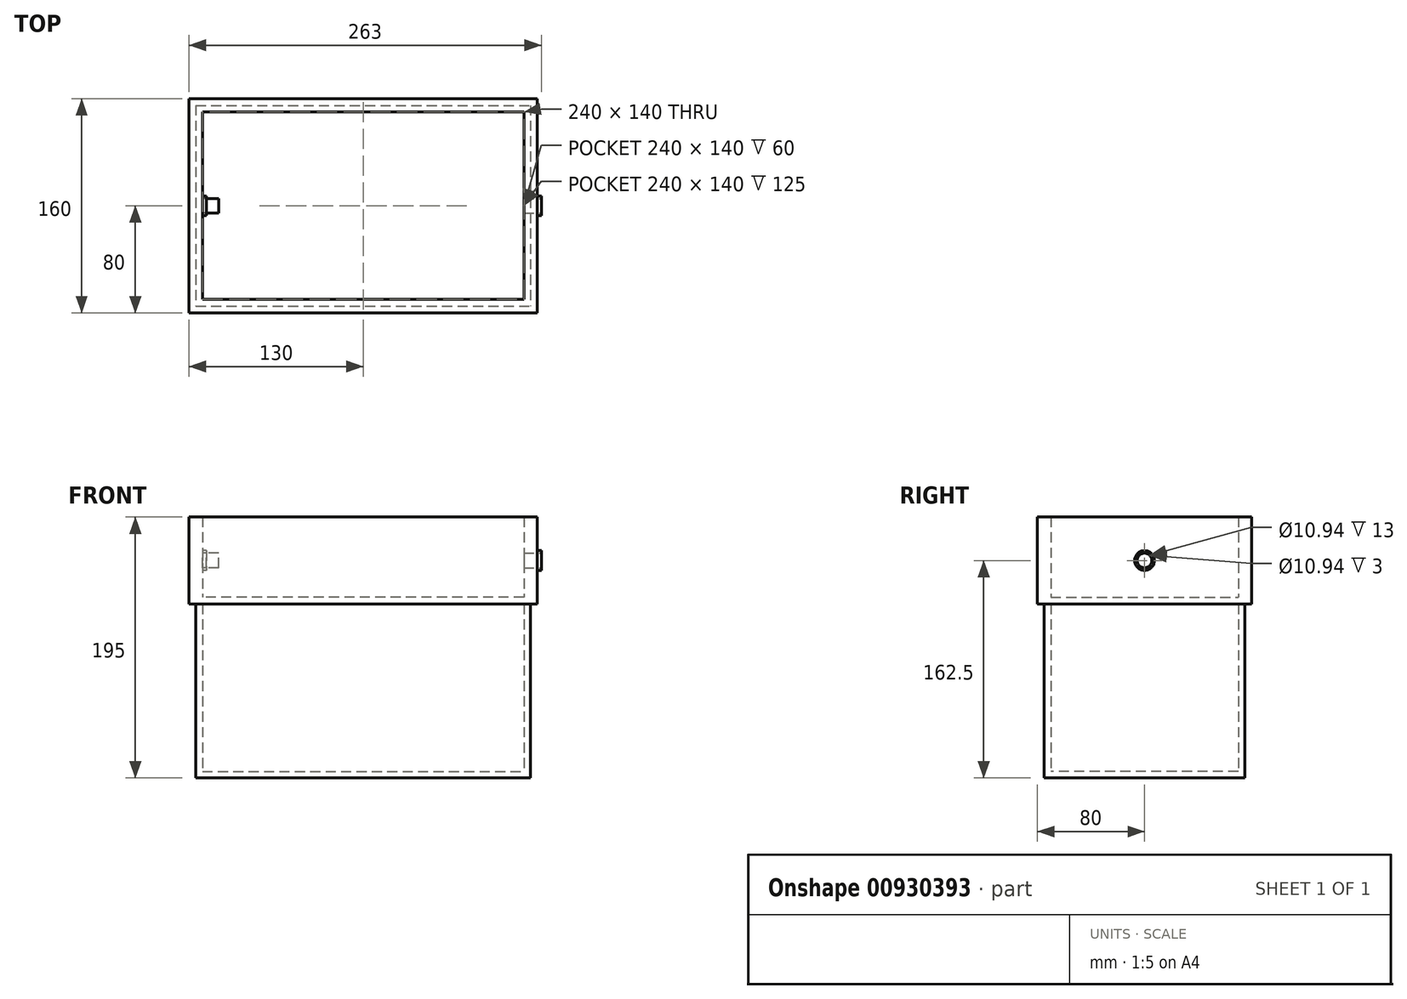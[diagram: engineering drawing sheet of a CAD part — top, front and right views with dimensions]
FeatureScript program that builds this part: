
annotation { "Feature Type Name" : "Feature", "Feature Type Description" : "" }
export const myFeature = defineFeature(function(context is Context, id is Id, definition is map)
    precondition{}
    {
        {
            var Q0;
            Q0=qCreatedBy(makeId("Top.planeOp"),FACE);
            var sketch = newSketch(context, id + "F0", { "sketchPlane" : qUnion([Q0])});
            skLineSegment(sketch, "E0.bottom", {"start": v(-125, 75) * mm, "end": v(125, 75) * mm});
            skLineSegment(sketch, "E0.top", {"start": v(-125, -75) * mm, "end": v(125, -75) * mm});
            skLineSegment(sketch, "E0.left", {"start": v(-125, 75) * mm, "end": v(-125, -75) * mm});
            skLineSegment(sketch, "E0.right", {"start": v(125, 75) * mm, "end": v(125, -75) * mm});
            skPoint(sketch, "E0.middle", {"position": v(0, 0) * mm});
            skSolve(sketch);
        }
        {
            var Q0;
            Q0 = qSketchRegion(id + "F0", true);
            extrude(context, id + "F1", {"entities" : qUnion([Q0]), "depth" : 5 * mm, "offsetDistance" : 25 * mm});
        }
        {
            var Q0;
            Q0=makeQuery(id+"F1.opExtrude","CAP_FACE",FACE,{"disambiguationData":[OSD([sQuery(id+"F0.wireOp",EDGE,"E0.bottom"),sQuery(id+"F0.wireOp",EDGE,"E0.top"),sQuery(id+"F0.wireOp",EDGE,"E0.left"),sQuery(id+"F0.wireOp",EDGE,"E0.right")])],"isStart":false});
            var sketch = newSketch(context, id + "F2", { "sketchPlane" : qUnion([Q0])});
            skLineSegment(sketch, "E1.bottom", {"start": v(-120, 70) * mm, "end": v(120, 70) * mm});
            skLineSegment(sketch, "E1.top", {"start": v(-120, -70) * mm, "end": v(120, -70) * mm});
            skLineSegment(sketch, "E1.left", {"start": v(-120, 70) * mm, "end": v(-120, -70) * mm});
            skLineSegment(sketch, "E1.right", {"start": v(120, 70) * mm, "end": v(120, -70) * mm});
            skPoint(sketch, "E1.middle", {"position": v(0, 0) * mm});
            skLineSegment(sketch, "E2.bottom", {"start": v(-125, 75) * mm, "end": v(125, 75) * mm});
            skLineSegment(sketch, "E2.top", {"start": v(-125, -75) * mm, "end": v(125, -75) * mm});
            skLineSegment(sketch, "E2.left", {"start": v(-125, 75) * mm, "end": v(-125, -75) * mm});
            skLineSegment(sketch, "E2.right", {"start": v(125, 75) * mm, "end": v(125, -75) * mm});
            skSolve(sketch);
        }
        {
            var Q0;
            Q0 = qSketchRegion(id + "F2", true);
            extrude(context, id + "F3", {"entities" : qUnion([Q0]), "operationType" : NewBodyOperationType.ADD, "depth" : 125 * mm, "offsetDistance" : 25 * mm});
        }
        {
            var Q0;
            Q0=makeQuery(id+"F3.opExtrude","CAP_FACE",FACE,{"disambiguationData":[OSD([sQuery(id+"F2.wireOp",EDGE,"E1.bottom"),sQuery(id+"F2.wireOp",EDGE,"E1.top"),sQuery(id+"F2.wireOp",EDGE,"E1.left"),sQuery(id+"F2.wireOp",EDGE,"E1.right"),sQuery(id+"F2.wireOp",EDGE,"E2.bottom"),sQuery(id+"F2.wireOp",EDGE,"E2.top"),sQuery(id+"F2.wireOp",EDGE,"E2.left"),sQuery(id+"F2.wireOp",EDGE,"E2.right")])],"isStart":false});
            var sketch = newSketch(context, id + "F4", { "sketchPlane" : qUnion([Q0])});
            skLineSegment(sketch, "E3.bottom", {"start": v(-130, 80) * mm, "end": v(130, 80) * mm});
            skLineSegment(sketch, "E3.top", {"start": v(-130, -80) * mm, "end": v(130, -80) * mm});
            skLineSegment(sketch, "E3.left", {"start": v(-130, 80) * mm, "end": v(-130, -80) * mm});
            skLineSegment(sketch, "E3.right", {"start": v(130, 80) * mm, "end": v(130, -80) * mm});
            skPoint(sketch, "E3.middle", {"position": v(0, 0) * mm});
            skSolve(sketch);
        }
        {
            var Q0;
            Q0 = qSketchRegion(id + "F4", true);
            extrude(context, id + "F5", {"entities" : qUnion([Q0]), "depth" : 5 * mm, "offsetDistance" : 25 * mm});
        }
        {
            var Q0;
            Q0=makeQuery(id+"F5.opExtrude","CAP_FACE",FACE,{"disambiguationData":[OSD([sQuery(id+"F4.wireOp",EDGE,"E3.bottom"),sQuery(id+"F4.wireOp",EDGE,"E3.top"),sQuery(id+"F4.wireOp",EDGE,"E3.left"),sQuery(id+"F4.wireOp",EDGE,"E3.right")])],"isStart":false});
            var sketch = newSketch(context, id + "F6", { "sketchPlane" : qUnion([Q0])});
            skLineSegment(sketch, "E4.bottom", {"start": v(130, -80) * mm, "end": v(-130, -80) * mm});
            skLineSegment(sketch, "E4.top", {"start": v(130, 80) * mm, "end": v(-130, 80) * mm});
            skLineSegment(sketch, "E4.left", {"start": v(130, -80) * mm, "end": v(130, 80) * mm});
            skLineSegment(sketch, "E4.right", {"start": v(-130, -80) * mm, "end": v(-130, 80) * mm});
            skPoint(sketch, "E4.middle", {"position": v(0, 0) * mm});
            skLineSegment(sketch, "E5.bottom", {"start": v(120, -70) * mm, "end": v(-120, -70) * mm});
            skLineSegment(sketch, "E5.top", {"start": v(120, 70) * mm, "end": v(-120, 70) * mm});
            skLineSegment(sketch, "E5.left", {"start": v(120, -70) * mm, "end": v(120, 70) * mm});
            skLineSegment(sketch, "E5.right", {"start": v(-120, -70) * mm, "end": v(-120, 70) * mm});
            skSolve(sketch);
        }
        {
            var Q0;
            Q0 = qSketchRegion(id + "F6", true);
            extrude(context, id + "F7", {"entities" : qUnion([Q0]), "operationType" : NewBodyOperationType.ADD, "depth" : 60 * mm, "offsetDistance" : 25 * mm});
        }
        {
            var Q0;
            Q0=makeQuery(id+"F7.boolean.opBoolean","MERGE",FACE,{"derivedFrom":[makeQuery(id+"F5.opExtrude","SWEPT_FACE",FACE,{"disambiguationData":[OSD([sQuery(id+"F4.wireOp",EDGE,"E3.right")])]}),makeQuery(id+"F7.opExtrude","SWEPT_FACE",FACE,{"disambiguationData":[OSD([sQuery(id+"F6.wireOp",EDGE,"E4.left")])]})]});
            var sketch = newSketch(context, id + "F8", { "sketchPlane" : qUnion([Q0])});
            skCircle(sketch, "E6", {"center": v(0, 162.5) * mm, "radius": 5.47 * mm});
            skPoint(sketch, "E6.centerSnap0", {"position": v(-80, 162.5) * mm});
            skPoint(sketch, "E6.centerSnap1", {"position": v(0, 130) * mm});
            skSolve(sketch);
        }
        {
            var Q0;
            Q0 = qSketchRegion(id + "F8", true);
            extrude(context, id + "F9", {"entities" : qUnion([Q0]), "operationType" : NewBodyOperationType.REMOVE, "oppositeDirection" : true, "depth" : 25 * mm, "offsetDistance" : 25 * mm});
        }
        {
            var Q0;
            Q0=makeQuery(id+"F7.boolean.opBoolean","MERGE",FACE,{"derivedFrom":[makeQuery(id+"F5.opExtrude","SWEPT_FACE",FACE,{"disambiguationData":[OSD([sQuery(id+"F4.wireOp",EDGE,"E3.right")])]}),makeQuery(id+"F7.opExtrude","SWEPT_FACE",FACE,{"disambiguationData":[OSD([sQuery(id+"F6.wireOp",EDGE,"E4.left")])]})]});
            var sketch = newSketch(context, id + "F10", { "sketchPlane" : qUnion([Q0])});
            skCircle(sketch, "E7", {"center": v(0, 162.5) * mm, "radius": 7.36 * mm});
            skCircle(sketch, "E8", {"center": v(0, 162.5) * mm, "radius": 5.44 * mm});
            skSolve(sketch);
        }
        {
            var Q0;
            Q0=makeQuery(id+"F10.imprint","IMPRINT",FACE,{"disambiguationData":[TD([[makeQuery(id+"F10.imprint","IMPRINT",EDGE,{"derivedFrom":sQuery(id+"F10.wireOp",EDGE,"E7")}),1.0]])]});
            extrude(context, id + "F11", {"entities" : qUnion([Q0]), "operationType" : NewBodyOperationType.ADD, "depth" : 3 * mm, "offsetDistance" : 25 * mm});
        }
        {
            var Q0;
            Q0=makeQuery(id+"F7.opExtrude","SWEPT_FACE",FACE,{"disambiguationData":[OSD([sQuery(id+"F6.wireOp",EDGE,"E5.right")])]});
            var sketch = newSketch(context, id + "F12", { "sketchPlane" : qUnion([Q0])});
            skCircle(sketch, "E9.0", {"center": v(0, 162.5) * mm, "radius": 7.36 * mm});
            skCircle(sketch, "E10.0", {"center": v(0, 162.5) * mm, "radius": 5.47 * mm});
            skSolve(sketch);
        }
        {
            var Q0;
            Q0 = qSketchRegion(id + "F12", true);
            extrude(context, id + "F13", {"entities" : qUnion([Q0]), "operationType" : NewBodyOperationType.ADD, "depth" : 3 * mm, "offsetDistance" : 25 * mm});
        }
        {
            var Q0;
            Q0=makeQuery(id+"F13.boolean.opBoolean","SPLIT",FACE,{"disambiguationData":[TD([makeQuery(id+"F13.opExtrude","SWEPT_FACE",FACE,{"disambiguationData":[OSD([sQuery(id+"F12.wireOp",EDGE,"E10.0")])]})])],"derivedFrom":makeQuery(id+"F7.opExtrude","SWEPT_FACE",FACE,{"disambiguationData":[OSD([sQuery(id+"F6.wireOp",EDGE,"E5.right")])]})});
            var sketch = newSketch(context, id + "F14", { "sketchPlane" : qUnion([Q0])});
            skSolve(sketch);
        }
        {
            var Q0;
            Q0=makeQuery(id+"F14.imprint","IMPRINT",FACE,{"disambiguationData":[TD([[makeQuery(id+"F14.imprint","IMPRINT",EDGE,{"derivedFrom":makeQuery(id+"F13.opExtrude","CAP_EDGE",EDGE,{"disambiguationData":[OSD([sQuery(id+"F12.wireOp",EDGE,"E10.0")])],"isStart":true})}),1.0]])]});
            var sketch = newSketch(context, id + "F15", { "sketchPlane" : qUnion([Q0])});
            skCircle(sketch, "E11.0.0", {"center": v(0, 162.5) * mm, "radius": 5.47 * mm});
            skSolve(sketch);
        }
        {
            var Q0;
            Q0 = qSketchRegion(id + "F15", true);
            extrude(context, id + "F16", {"entities" : qUnion([Q0]), "depth" : 12 * mm, "offsetDistance" : 25 * mm});
        }
    });
